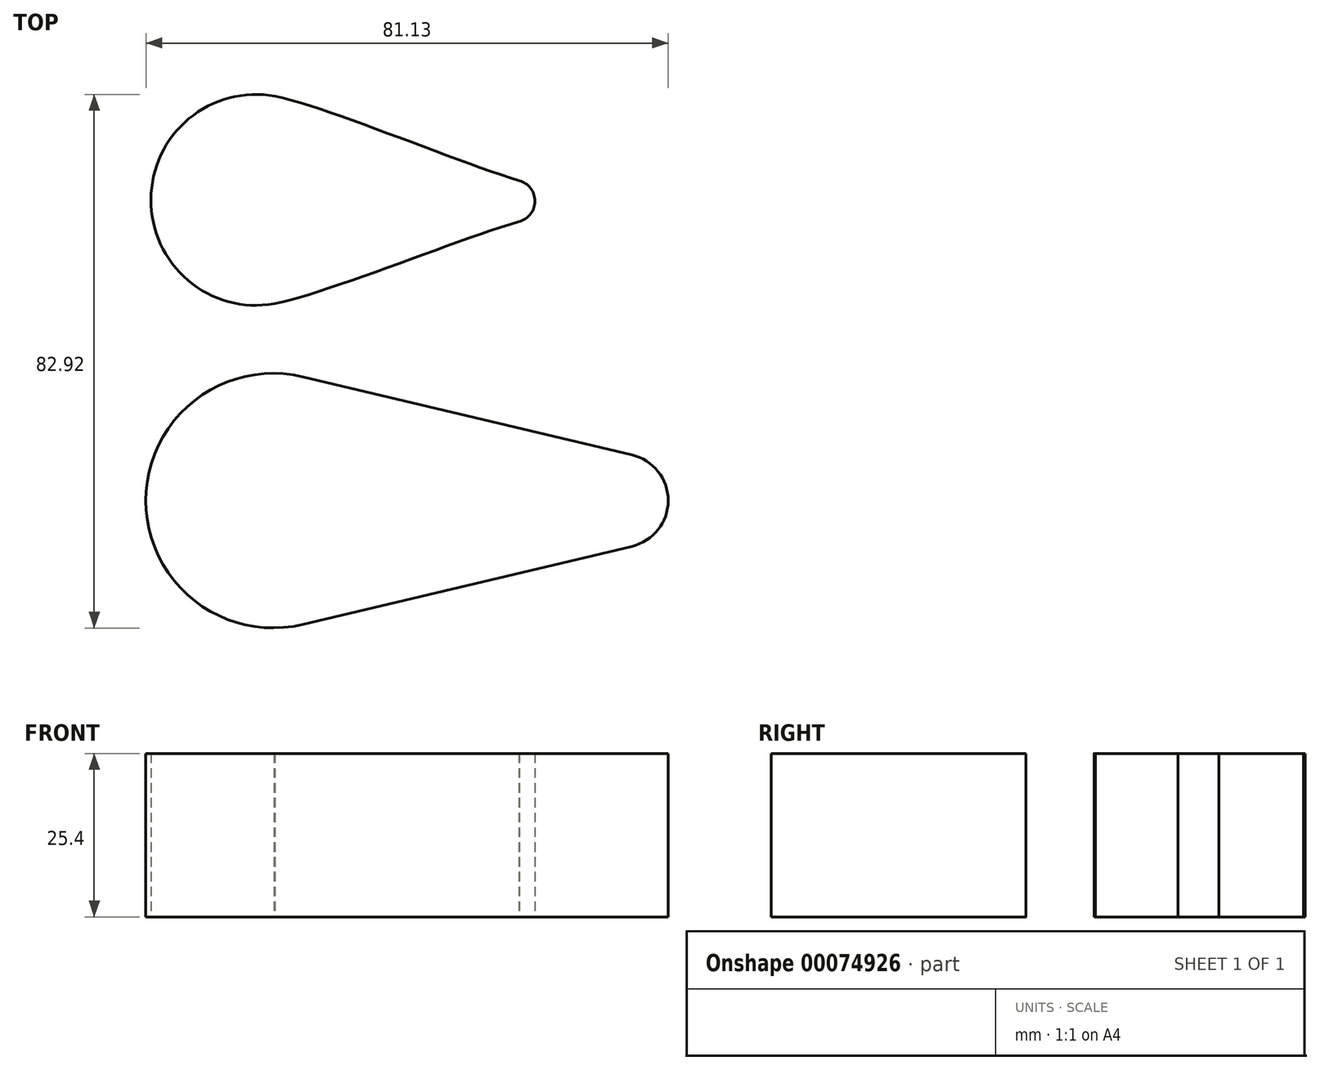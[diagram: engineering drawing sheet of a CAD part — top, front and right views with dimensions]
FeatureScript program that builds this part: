
annotation { "Feature Type Name" : "Feature", "Feature Type Description" : "" }
export const myFeature = defineFeature(function(context is Context, id is Id, definition is map)
    precondition{}
    {
        {
            var Q0;
            Q0=qCreatedBy(makeId("Top.planeOp"),FACE);
            var sketch = newSketch(context, id + "F0", { "sketchPlane" : qUnion([Q0])});
            skArc(sketch, "E0", {"start": v(1.69, -7.1) * mm, "mid": v(7.3, 0) * mm, "end": v(1.69, 7.1) * mm});
            skArc(sketch, "E1", {"start": v(-49.48, 19.25) * mm, "mid": v(-73.83, 0) * mm, "end": v(-49.48, -19.25) * mm});
            skLineSegment(sketch, "E2", {"start": v(-49.48, 19.25) * mm, "end": v(1.69, 7.1) * mm});
            skLineSegment(sketch, "E3.MirrorCS", {"start": v(-49.48, -19.25) * mm, "end": v(1.69, -7.1) * mm});
            skSolve(sketch);
        }
        {
            var Q0;
            Q0=qCreatedBy(makeId("Top.planeOp"),FACE);
            var sketch = newSketch(context, id + "F1", { "sketchPlane" : qUnion([Q0])});
            skArc(sketch, "E4", {"start": v(-53.8, 62.86) * mm, "mid": v(-67.17, 59.34) * mm, "end": v(-73.03, 46.81) * mm});
            skArc(sketch, "E5", {"start": v(-13.4, 46.53) * mm, "mid": v(-14.09, 48.54) * mm, "end": v(-15.85, 49.73) * mm});
            skFitSpline(sketch, "E6", {"points": [v(-53.8, 62.86) * mm, v(-15.85, 49.73) * mm], "startDerivative": vector(26.27, -5.63) * mm, "endDerivative": vector(30.86, -9.38) * mm});
            skLineSegment(sketch, "E7", {"start": v(-56.72, 46.81) * mm, "end": v(-73.03, 46.81) * mm});
            skLineSegment(sketch, "E8", {"start": v(-73.03, 46.81) * mm, "end": v(-13.4, 46.53) * mm});
            skFitSpline(sketch, "E9.MirrorCS", {"points": [v(-53.95, 30.58) * mm, v(-15.88, 43.36) * mm], "startDerivative": vector(26.32, 5.38) * mm, "endDerivative": vector(30.95, 9.09) * mm});
            skArc(sketch, "E10.MirrorCS", {"start": v(-13.4, 46.53) * mm, "mid": v(-14.1, 44.52) * mm, "end": v(-15.88, 43.36) * mm});
            skArc(sketch, "E11.MirrorCS", {"start": v(-53.95, 30.58) * mm, "mid": v(-67.29, 34.23) * mm, "end": v(-73.03, 46.81) * mm});
            skPoint(sketch, "E12.0.internal.orphan", {"position": v(0, 46.56) * mm});
            skPoint(sketch, "E12.2.internal.orphan", {"position": v(0, -85.52) * mm});
            skSolve(sketch);
        }
        {
            var Q0;
            Q0=makeQuery(id+"F1.imprint","IMPRINT",FACE,{"disambiguationData":[TD([[makeQuery(id+"F1.imprint","IMPRINT",EDGE,{"derivedFrom":sQuery(id+"F1.wireOp",EDGE,"E8")}),-1.0]])]});
            var Q1;
            Q1=makeQuery(id+"F1.imprint","IMPRINT",FACE,{"disambiguationData":[TD([[makeQuery(id+"F1.imprint","IMPRINT",EDGE,{"derivedFrom":sQuery(id+"F1.wireOp",EDGE,"E4")}),1.0]])]});
            extrude(context, id + "F2", {"entities" : qUnion([Q0, Q1]), "depth" : 25.4 * mm});
        }
        {
            var Q0;
            Q0 = qSketchRegion(id + "F0", true);
            extrude(context, id + "F3", {"entities" : qUnion([Q0]), "depth" : 25.4 * mm});
        }
    });
